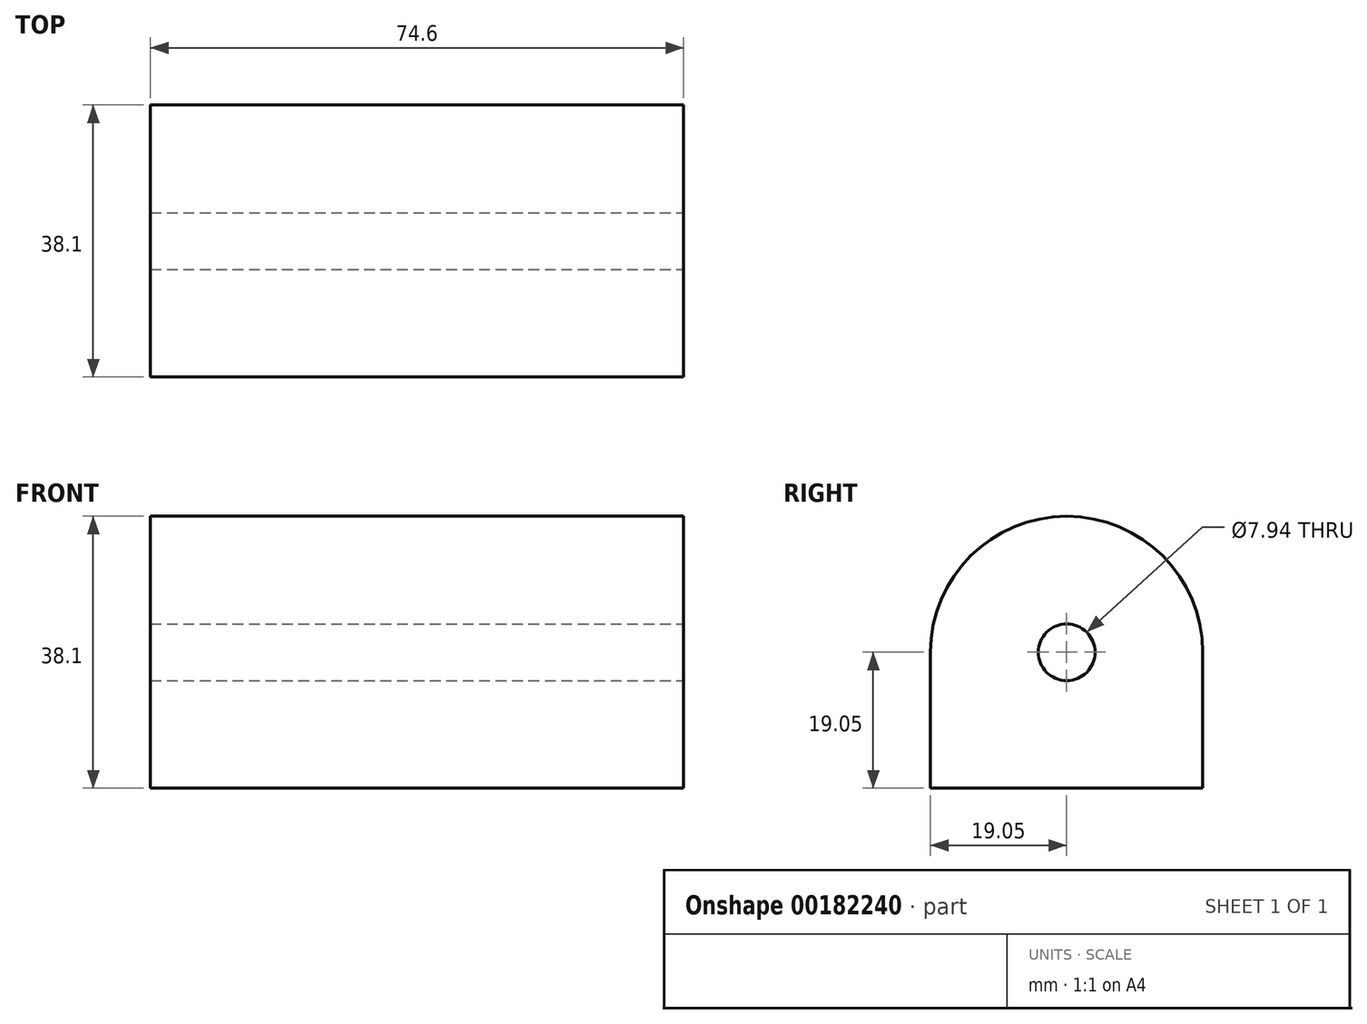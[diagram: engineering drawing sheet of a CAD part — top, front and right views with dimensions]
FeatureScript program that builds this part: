
annotation { "Feature Type Name" : "Feature", "Feature Type Description" : "" }
export const myFeature = defineFeature(function(context is Context, id is Id, definition is map)
    precondition{}
    {
        {
            var Q0;
            Q0=qCreatedBy(makeId("Right.planeOp"),FACE);
            var sketch = newSketch(context, id + "F0", { "sketchPlane" : qUnion([Q0])});
            skLineSegment(sketch, "E0.bottom", {"start": v(0, 0) * mm, "end": v(38.1, 0) * mm});
            skLineSegment(sketch, "E0.left", {"start": v(0, 0) * mm, "end": v(0, 19.05) * mm});
            skLineSegment(sketch, "E0.right", {"start": v(38.1, 0) * mm, "end": v(38.1, 19.05) * mm});
            skArc(sketch, "E1", {"start": v(0, 19.05) * mm, "mid": v(19.05, 38.1) * mm, "end": v(38.1, 19.05) * mm});
            skCircle(sketch, "E2", {"center": v(19.05, 19.05) * mm, "radius": 3.97 * mm});
            skSolve(sketch);
        }
        {
            var Q0;
            Q0=qSketchRegion(id+"F0",true);
            extrude(context, id + "F1", {"entities" : qUnion([Q0]), "oppositeDirection" : true, "depth" : 74.6 * mm});
        }
    });
